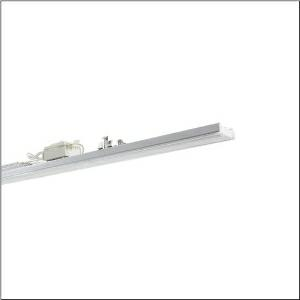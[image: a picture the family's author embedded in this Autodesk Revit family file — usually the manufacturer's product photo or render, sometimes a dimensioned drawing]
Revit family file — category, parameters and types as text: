
# Revit family: licross_r__11_recessed_mo_51tl1edn495g_457b
name_source: partatom
category: Lighting Fixtures
units: mm (PartAtom-declared; Revit-internal decimal feet)

## family parameters
Cut with Voids When Loaded = No
Host = Face
Light Source = No
Part Type = Normal
Room Calculation Point = No
Round Connector Dimension = Use Diameter
Shared = No

## types (1)
- --- (1 x LED, 9900 lm, 56.7 W, 4000K)
    Apparent Load = 57 VA
    CIE Flux Codes = 85 95 99 100 100
    Color Rendering = 80
    Color Temperature = 4000K
    Default Elevation = 1800 mm
    Description = Licross® 11 Recessed MO, luminaire insert, of sheet steel, coil coated, white, length: 1.500mm, width: 66mm, height: 67mm, LED rated luminous flux: 9.900lm, light colour: 840, control gear: DALI 2, with plug, 5-pole, with phase selection, mains connection: 220..240V, AC, 50/60Hz, rated input power: 57W, internal wiring halogen-free, primary light control with lens, of plastic, primary optical cover: cover, of PMMA, light emission: direct distribution, primary light characteristic: symmetric, protection rating (complete): IP40, insulation class (complete): insulation class I (protective earthing), certification: CE, ENEC, VDE, UKCA, protection symbol: D if used in an environment without relevant dust loads with corresponding accessories, impact resistance: IK06, permissible ambient temperature for indoor applications: -25..+35°C, corresponds to IFS (International Featured Standards) requirements for safety and quality in the food industry, reducing of maximum allowable ambient temperature of 5°C with ceiling mounting, LABS conformity tested according to VDMA 24364:2018-05, packaging unit: 1 piece
    Height = 58 mm
    Lamp = 1 x LED
    Lamp Light Flux = 9900 lm
    Lamp Power = 56.7 W
    Lamp count = 1
    Length = 1500 mm
    Luminous efficacy = 175 lm/W
    Manufacturer = Siteco
    ModVariant = No
    Model = 51TL1EDN495G
    Mounting Place = Ceiling
    Mounting Type = Pendant
    Number of Poles = 1
    OnlyDefault = Yes
    Power Factor = 1
    Product Name = Licross® 11 Recessed MO
    Product group = luminaire insert | ceiling pendant
    ProductGroupID = 902
    Protection Class = Protection class I
    Protection Degree = IP 40
    RLX_Detail_Level = 1
    RLX_Emergency_Light_Flux = 0 lm
    RLX_Emergency_Type = 0
    RLX_Emergency_Type_DB = No
    RlxData = <blob elided: 24657 chars, md5=325d7233>
    Socket = socket
    Standby Power = 0 W
    System Light Flux = 9900 lm
    System Power = 57 W
    Type Comments = factory setting: luminous flux: 100 % | dim-lin: 254 | 378 mA
    Type Image = l_1296930.jpg
    URL = http://relux.com
    VarID = @adj_117563
    Voltage = 0 V
    Weight = 0.00 kg
    Width = 66 mm

## geometry (parser evidence)
native form markers: Blend x4, Sweep x12
no freeform markers — native parametric forms only
